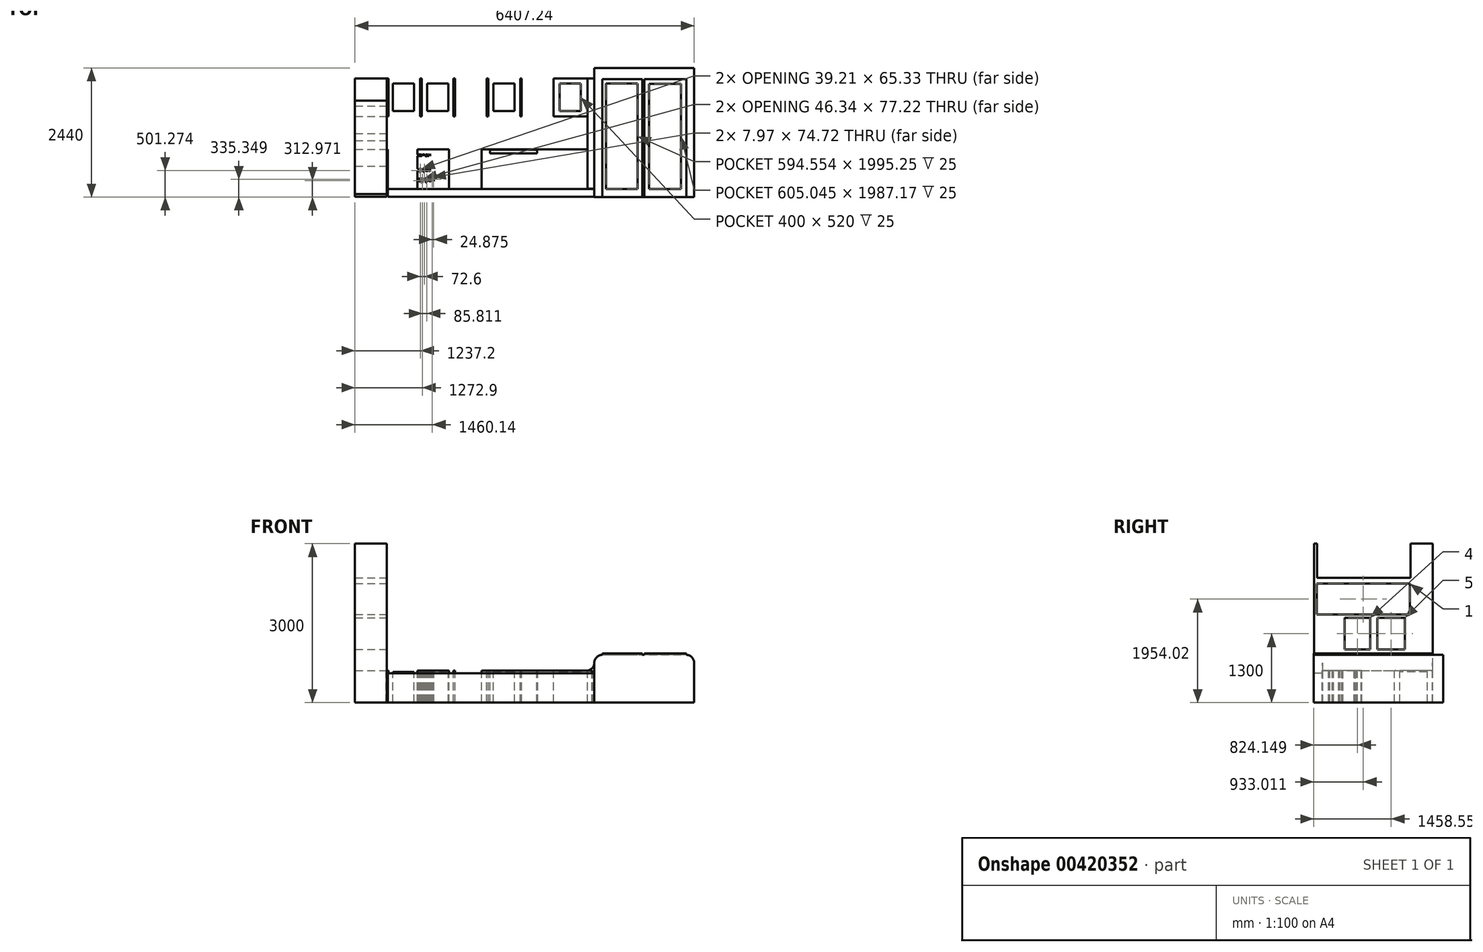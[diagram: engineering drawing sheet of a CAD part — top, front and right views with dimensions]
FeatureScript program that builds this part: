
annotation { "Feature Type Name" : "Feature", "Feature Type Description" : "" }
export const myFeature = defineFeature(function(context is Context, id is Id, definition is map)
    precondition{}
    {
        {
            var Q0;
            Q0=qCreatedBy(makeId("Top.planeOp"),FACE);
            var sketch = newSketch(context, id + "F0", { "sketchPlane" : qUnion([Q0])});
            skLineSegment(sketch, "E0.bottom", {"start": v(0, 750) * mm, "end": v(1806, 750) * mm});
            skLineSegment(sketch, "E0.top", {"start": v(0, 0) * mm, "end": v(3890, 0) * mm});
            skLineSegment(sketch, "E0.left", {"start": v(0, 750) * mm, "end": v(0, 0) * mm});
            skLineSegment(sketch, "E0.right", {"start": v(3890, 750) * mm, "end": v(3890, 0) * mm});
            skLineSegment(sketch, "E1.bottom", {"start": v(1190, 750) * mm, "end": v(1790, 750) * mm});
            skLineSegment(sketch, "E1.top", {"start": v(1190, 0) * mm, "end": v(1790, 0) * mm});
            skLineSegment(sketch, "E1.left", {"start": v(1190, 750) * mm, "end": v(1190, 0) * mm});
            skLineSegment(sketch, "E1.right", {"start": v(1790, 750) * mm, "end": v(1790, 0) * mm});
            skLineSegment(sketch, "E2.bottom", {"start": v(600, 740) * mm, "end": v(1164, 740) * mm});
            skLineSegment(sketch, "E2.top", {"start": v(600, 590) * mm, "end": v(1164, 590) * mm});
            skLineSegment(sketch, "E2.left", {"start": v(600, 740) * mm, "end": v(600, 590) * mm});
            skLineSegment(sketch, "E2.right", {"start": v(1164, 740) * mm, "end": v(1164, 590) * mm});
            skLineSegment(sketch, "E3.bottom", {"start": v(600, 560) * mm, "end": v(1164, 560) * mm});
            skLineSegment(sketch, "E3.top", {"start": v(600, 300) * mm, "end": v(1164, 300) * mm});
            skLineSegment(sketch, "E3.left", {"start": v(600, 560) * mm, "end": v(600, 300) * mm});
            skLineSegment(sketch, "E3.right", {"start": v(1164, 560) * mm, "end": v(1164, 300) * mm});
            skLineSegment(sketch, "E4.bottom", {"start": v(600, 270) * mm, "end": v(1164, 270) * mm});
            skLineSegment(sketch, "E4.top", {"start": v(600, 10) * mm, "end": v(1164, 10) * mm});
            skLineSegment(sketch, "E4.left", {"start": v(600, 270) * mm, "end": v(600, 10) * mm});
            skLineSegment(sketch, "E4.right", {"start": v(1164, 270) * mm, "end": v(1164, 10) * mm});
            skLineSegment(sketch, "E5.top", {"start": v(1816, 590) * mm, "end": v(2843, 590) * mm});
            skLineSegment(sketch, "E5.left", {"start": v(1816, 740) * mm, "end": v(1816, 590) * mm});
            skLineSegment(sketch, "E5.right", {"start": v(2843, 740) * mm, "end": v(2843, 590) * mm});
            skLineSegment(sketch, "E6.top", {"start": v(1816, 300) * mm, "end": v(2843, 300) * mm});
            skLineSegment(sketch, "E6.right", {"start": v(2843, 750) * mm, "end": v(2843, 590) * mm});
            skLineSegment(sketch, "E7.bottom", {"start": v(1826, 270) * mm, "end": v(2843, 270) * mm});
            skLineSegment(sketch, "E7.top", {"start": v(1826, 10) * mm, "end": v(2843, 10) * mm});
            skLineSegment(sketch, "E7.left", {"start": v(1826, 270) * mm, "end": v(1826, 10) * mm});
            skLineSegment(sketch, "E7.right", {"start": v(2843, 270) * mm, "end": v(2843, 10) * mm});
            skLineSegment(sketch, "E8.bottom", {"start": v(2853, 740) * mm, "end": v(3880, 740) * mm});
            skLineSegment(sketch, "E8.top", {"start": v(2853, 590) * mm, "end": v(3880, 590) * mm});
            skLineSegment(sketch, "E8.left", {"start": v(2853, 740) * mm, "end": v(2853, 590) * mm});
            skLineSegment(sketch, "E9.bottom", {"start": v(2853, 560) * mm, "end": v(3880, 560) * mm});
            skLineSegment(sketch, "E9.top", {"start": v(2853, 300) * mm, "end": v(3880, 300) * mm});
            skLineSegment(sketch, "E9.left", {"start": v(2853, 560) * mm, "end": v(2853, 300) * mm});
            skLineSegment(sketch, "E9.right", {"start": v(3880, 560) * mm, "end": v(3880, 300) * mm});
            skLineSegment(sketch, "E10.bottom", {"start": v(2853, 270) * mm, "end": v(3880, 270) * mm});
            skLineSegment(sketch, "E10.top", {"start": v(2853, 10) * mm, "end": v(3880, 10) * mm});
            skLineSegment(sketch, "E10.left", {"start": v(2853, 270) * mm, "end": v(2853, 10) * mm});
            skLineSegment(sketch, "E10.right", {"start": v(3880, 270) * mm, "end": v(3880, 10) * mm});
            skLineSegment(sketch, "E11.bottom", {"start": v(12.85, 1370) * mm, "end": v(3902.85, 1370) * mm});
            skLineSegment(sketch, "E11.top", {"start": v(12.85, 2090) * mm, "end": v(3902.85, 2090) * mm});
            skLineSegment(sketch, "E11.left", {"start": v(12.85, 1370) * mm, "end": v(12.85, 2090) * mm});
            skLineSegment(sketch, "E11.right", {"start": v(3902.85, 1370) * mm, "end": v(3902.85, 2090) * mm});
            skText(sketch, "E12", { "text": "Dishwasher", "fontName": "OpenSans-Regular.ttf"});
            skLineSegment(sketch, "E13", {"start": v(1174, 750) * mm, "end": v(1174, 0) * mm});
            skLineSegment(sketch, "E14", {"start": v(1806, 750) * mm, "end": v(1806, 0) * mm});
            skLineSegment(sketch, "E15", {"start": v(1816, 740) * mm, "end": v(2843, 740) * mm});
            skLineSegment(sketch, "E16", {"start": v(3890, 750) * mm, "end": v(1806, 750) * mm});
            skLineSegment(sketch, "E17", {"start": v(3880, 590) * mm, "end": v(3880, 740) * mm});
            skLineSegment(sketch, "E18", {"start": v(1816, 300) * mm, "end": v(1816, 560) * mm});
            skLineSegment(sketch, "E19", {"start": v(1816, 560) * mm, "end": v(2843, 560) * mm});
            skLineSegment(sketch, "E20.trimOffspring", {"start": v(2843, 560) * mm, "end": v(2843, 300) * mm});
            skLineSegment(sketch, "E21.bottom", {"start": v(42.85, 2090) * mm, "end": v(642.85, 2090) * mm});
            skLineSegment(sketch, "E21.top", {"start": v(42.85, 1370) * mm, "end": v(642.85, 1370) * mm});
            skLineSegment(sketch, "E21.left", {"start": v(42.85, 2090) * mm, "end": v(42.85, 1370) * mm});
            skLineSegment(sketch, "E21.right", {"start": v(642.85, 2090) * mm, "end": v(642.85, 1370) * mm});
            skLineSegment(sketch, "E22", {"start": v(6000, -150) * mm, "end": v(6000, 2090) * mm, "construction": true});
            skPoint(sketch, "E23", {"position": v(6000, 0) * mm});
            skPoint(sketch, "E24", {"position": v(6000, 1370) * mm});
            skPoint(sketch, "E25", {"position": v(6000, 750) * mm});
            skPoint(sketch, "E26", {"position": v(6000, 770) * mm});
            skLineSegment(sketch, "E27", {"start": v(6000, 2090) * mm, "end": v(5702.85, 2090) * mm, "construction": true});
            skLineSegment(sketch, "E28", {"start": v(6000, 2090) * mm, "end": v(6000, 2090) * mm});
            skLineSegment(sketch, "E29.bottom", {"start": v(672.85, 2090) * mm, "end": v(1272.85, 2090) * mm});
            skLineSegment(sketch, "E29.top", {"start": v(672.85, 1370) * mm, "end": v(1272.85, 1370) * mm});
            skLineSegment(sketch, "E29.left", {"start": v(672.85, 2090) * mm, "end": v(672.85, 1370) * mm});
            skLineSegment(sketch, "E29.right", {"start": v(1272.85, 2090) * mm, "end": v(1272.85, 1370) * mm});
            skLineSegment(sketch, "E30.bottom", {"start": v(1302.85, 2090) * mm, "end": v(1902.85, 2090) * mm});
            skLineSegment(sketch, "E30.top", {"start": v(1302.85, 1370) * mm, "end": v(1902.85, 1370) * mm});
            skLineSegment(sketch, "E30.left", {"start": v(1302.85, 2090) * mm, "end": v(1302.85, 1370) * mm});
            skLineSegment(sketch, "E30.right", {"start": v(1902.85, 2090) * mm, "end": v(1902.85, 1370) * mm});
            skLineSegment(sketch, "E31.bottom", {"start": v(1932.85, 2090) * mm, "end": v(2532.85, 2090) * mm});
            skLineSegment(sketch, "E31.top", {"start": v(1932.85, 1370) * mm, "end": v(2532.85, 1370) * mm});
            skLineSegment(sketch, "E31.left", {"start": v(1932.85, 2090) * mm, "end": v(1932.85, 1370) * mm});
            skLineSegment(sketch, "E31.right", {"start": v(2532.85, 2090) * mm, "end": v(2532.85, 1370) * mm});
            skLineSegment(sketch, "E32.bottom", {"start": v(2562.85, 2090) * mm, "end": v(3162.85, 2090) * mm});
            skLineSegment(sketch, "E32.top", {"start": v(2562.85, 1370) * mm, "end": v(3162.85, 1370) * mm});
            skLineSegment(sketch, "E32.left", {"start": v(2562.85, 2090) * mm, "end": v(2562.85, 1370) * mm});
            skLineSegment(sketch, "E32.right", {"start": v(3162.85, 2090) * mm, "end": v(3162.85, 1370) * mm});
            skLineSegment(sketch, "E33.bottom", {"start": v(3162.85, 2090) * mm, "end": v(3192.85, 2090) * mm});
            skLineSegment(sketch, "E33.top", {"start": v(3162.85, 1370) * mm, "end": v(3192.85, 1370) * mm});
            skLineSegment(sketch, "E33.left", {"start": v(3192.85, 2090) * mm, "end": v(3192.85, 1370) * mm});
            skLineSegment(sketch, "E34.bottom", {"start": v(3192.85, 2090) * mm, "end": v(3792.85, 2090) * mm});
            skLineSegment(sketch, "E34.top", {"start": v(3192.85, 1370) * mm, "end": v(3792.85, 1370) * mm});
            skLineSegment(sketch, "E34.right", {"start": v(3792.85, 2090) * mm, "end": v(3792.85, 1370) * mm});
            skLineSegment(sketch, "E35.bottom", {"start": v(30, 750) * mm, "end": v(590, 750) * mm});
            skLineSegment(sketch, "E35.top", {"start": v(30, 0) * mm, "end": v(590, 0) * mm});
            skLineSegment(sketch, "E35.left", {"start": v(30, 750) * mm, "end": v(30, 0) * mm});
            skLineSegment(sketch, "E35.right", {"start": v(590, 750) * mm, "end": v(590, 0) * mm});
            skText(sketch, "E36", { "text": "Lemans II \n541.32.620", "fontName": "OpenSans-Regular.ttf"});
            skText(sketch, "E37", { "text": "Bottom pull", "fontName": "OpenSans-Regular.ttf"});
            skText(sketch, "E38", { "text": "top pull", "fontName": "OpenSans-Regular.ttf"});
            skText(sketch, "E39", { "text": "top pull", "fontName": "OpenSans-Regular.ttf"});
            skLineSegment(sketch, "E40", {"start": v(6000, -150) * mm, "end": v(0, -150) * mm, "construction": true});
            skLineSegment(sketch, "E41.bottom", {"start": v(3902.85, 2090) * mm, "end": v(5702.85, 2090) * mm});
            skLineSegment(sketch, "E41.top", {"start": v(3902.85, 0) * mm, "end": v(5702.85, 0) * mm});
            skLineSegment(sketch, "E41.left", {"start": v(3902.85, 2090) * mm, "end": v(3902.85, 0) * mm});
            skLineSegment(sketch, "E41.right", {"start": v(5702.85, 2090) * mm, "end": v(5702.85, 0) * mm});
            skLineSegment(sketch, "E42", {"start": v(4772.85, 2090) * mm, "end": v(4772.85, 0) * mm});
            skLineSegment(sketch, "E43", {"start": v(4802.85, 2090) * mm, "end": v(4802.85, 0) * mm});
            skLineSegment(sketch, "E44", {"start": v(3932.85, 2090) * mm, "end": v(3932.85, 0) * mm});
            skLineSegment(sketch, "E45.bottom", {"start": v(127.34, 1990) * mm, "end": v(527.34, 1990) * mm});
            skLineSegment(sketch, "E45.top", {"start": v(127.34, 1470) * mm, "end": v(527.34, 1470) * mm});
            skLineSegment(sketch, "E45.left", {"start": v(127.34, 1990) * mm, "end": v(127.34, 1470) * mm});
            skLineSegment(sketch, "E45.right", {"start": v(527.34, 1990) * mm, "end": v(527.34, 1470) * mm});
            skLineSegment(sketch, "E46.bottom", {"start": v(772.85, 1990) * mm, "end": v(1172.85, 1990) * mm});
            skLineSegment(sketch, "E46.top", {"start": v(772.85, 1470) * mm, "end": v(1172.85, 1470) * mm});
            skLineSegment(sketch, "E46.left", {"start": v(772.85, 1990) * mm, "end": v(772.85, 1470) * mm});
            skLineSegment(sketch, "E46.right", {"start": v(1172.85, 1990) * mm, "end": v(1172.85, 1470) * mm});
            skLineSegment(sketch, "E47.bottom", {"start": v(2028.05, 1990) * mm, "end": v(2428.05, 1990) * mm});
            skLineSegment(sketch, "E47.top", {"start": v(2028.05, 1470) * mm, "end": v(2428.05, 1470) * mm});
            skLineSegment(sketch, "E47.left", {"start": v(2028.05, 1990) * mm, "end": v(2028.05, 1470) * mm});
            skLineSegment(sketch, "E47.right", {"start": v(2428.05, 1990) * mm, "end": v(2428.05, 1470) * mm});
            skLineSegment(sketch, "E48.bottom", {"start": v(3280.66, 1990) * mm, "end": v(3680.66, 1990) * mm});
            skLineSegment(sketch, "E48.top", {"start": v(3280.66, 1470) * mm, "end": v(3680.66, 1470) * mm});
            skLineSegment(sketch, "E48.left", {"start": v(3280.66, 1990) * mm, "end": v(3280.66, 1470) * mm});
            skLineSegment(sketch, "E48.right", {"start": v(3680.66, 1990) * mm, "end": v(3680.66, 1470) * mm});
            skText(sketch, "E49", { "text": "Stove", "fontName": "OpenSans-Regular.ttf"});
            skPoint(sketch, "E50", {"position": v(2061.13, 1179.17) * mm});
            skPoint(sketch, "E51", {"position": v(2414.2, 750) * mm});
            skLineSegment(sketch, "E52.bottom", {"start": v(1964.2, 750) * mm, "end": v(2864.2, 750) * mm});
            skLineSegment(sketch, "E52.top", {"start": v(1964.2, 670) * mm, "end": v(2864.2, 670) * mm});
            skLineSegment(sketch, "E52.left", {"start": v(1964.2, 750) * mm, "end": v(1964.2, 670) * mm});
            skLineSegment(sketch, "E52.right", {"start": v(2864.2, 750) * mm, "end": v(2864.2, 670) * mm});
            skLineSegment(sketch, "E53.bottom", {"start": v(3932.85, 2090) * mm, "end": v(4091.6, 2090) * mm});
            skLineSegment(sketch, "E53.top", {"start": v(3932.85, -150) * mm, "end": v(4091.6, -150) * mm});
            skLineSegment(sketch, "E53.left", {"start": v(3932.85, 2090) * mm, "end": v(3932.85, -150) * mm});
            skLineSegment(sketch, "E53.right", {"start": v(4091.6, 2090) * mm, "end": v(4091.6, -150) * mm});
            skLineSegment(sketch, "E54.bottom", {"start": v(5586.52, 2090) * mm, "end": v(5820.09, 2090) * mm});
            skLineSegment(sketch, "E54.top", {"start": v(5586.52, -159.02) * mm, "end": v(5820.09, -159.02) * mm});
            skLineSegment(sketch, "E54.left", {"start": v(5586.52, 2090) * mm, "end": v(5586.52, -159.02) * mm});
            skLineSegment(sketch, "E54.right", {"start": v(5820.09, 2090) * mm, "end": v(5820.09, -159.02) * mm});
            skPoint(sketch, "E55.oppositeSnap0", {"position": v(5703.3, 2090) * mm});
            skLineSegment(sketch, "E55.bottom", {"start": v(3932.85, 2286.83) * mm, "end": v(5820.09, 2286.83) * mm});
            skLineSegment(sketch, "E55.top", {"start": v(3932.85, 2090) * mm, "end": v(5820.09, 2090) * mm});
            skLineSegment(sketch, "E55.left", {"start": v(3932.85, 2286.83) * mm, "end": v(3932.85, 2090) * mm});
            skLineSegment(sketch, "E55.right", {"start": v(5820.09, 2286.83) * mm, "end": v(5820.09, 2090) * mm});
            skLineSegment(sketch, "E56.trimOffspring", {"start": v(3932.85, 2090) * mm, "end": v(12.85, 2090) * mm, "construction": true});
            skLineSegment(sketch, "E57.trimOffspring", {"start": v(5586.52, 2090) * mm, "end": v(4091.6, 2090) * mm, "construction": true});
            skLineSegment(sketch, "E58.bottom", {"start": v(1405.73, 1990) * mm, "end": v(1817.16, 1990) * mm});
            skLineSegment(sketch, "E58.top", {"start": v(1405.73, 1470) * mm, "end": v(1817.16, 1470) * mm});
            skLineSegment(sketch, "E58.left", {"start": v(1405.73, 1990) * mm, "end": v(1405.73, 1470) * mm});
            skLineSegment(sketch, "E58.right", {"start": v(1817.16, 1990) * mm, "end": v(1817.16, 1470) * mm});
            skLineSegment(sketch, "E59.bottom", {"start": v(2646, 1990) * mm, "end": v(3066.6, 1990) * mm});
            skLineSegment(sketch, "E59.top", {"start": v(2646, 1470) * mm, "end": v(3066.6, 1470) * mm});
            skLineSegment(sketch, "E59.left", {"start": v(2646, 1990) * mm, "end": v(2646, 1470) * mm});
            skLineSegment(sketch, "E59.right", {"start": v(3066.6, 1990) * mm, "end": v(3066.6, 1470) * mm});
            skLineSegment(sketch, "E60.bottom", {"start": v(30, 0) * mm, "end": v(0, 0) * mm});
            skLineSegment(sketch, "E60.top", {"start": v(30, -150) * mm, "end": v(0, -150) * mm});
            skLineSegment(sketch, "E60.left", {"start": v(30, 0) * mm, "end": v(30, -150) * mm});
            skLineSegment(sketch, "E60.right", {"start": v(0, 0) * mm, "end": v(0, -150) * mm});
            skLineSegment(sketch, "E61.bottom", {"start": v(0, 0) * mm, "end": v(3932.85, 0) * mm});
            skLineSegment(sketch, "E61.top", {"start": v(0, -150) * mm, "end": v(3932.85, -150) * mm});
            skLineSegment(sketch, "E61.right", {"start": v(3932.85, 0) * mm, "end": v(3932.85, -150) * mm});
            skLineSegment(sketch, "E62.bottom", {"start": v(4091.6, 0) * mm, "end": v(5586.52, 0) * mm});
            skLineSegment(sketch, "E62.top", {"start": v(4091.6, -159.02) * mm, "end": v(5586.52, -159.02) * mm});
            skLineSegment(sketch, "E62.left", {"start": v(4091.6, 0) * mm, "end": v(4091.6, -159.02) * mm});
            skLineSegment(sketch, "E62.right", {"start": v(5586.52, 0) * mm, "end": v(5586.52, -159.02) * mm});
            const initialGuessF0  = {"E12": [1.29, 0.4978, 1, 0, 0.0522], "E36": [0.08, 0.61298, 1, 0, 0.04765], "E37": [0.54096, 0.62134, 1, 0, 0.03929], "E38": [0.54368, 0.33543, 1, 0, 0.0599], "E39": [0.56002, 0.14482, 1, 0, 0.0708], "E49": [1.91777, 1.09917, 1, 0, 0.08]};
            skSetInitialGuess(sketch, initialGuessF0);
            skSolve(sketch);
        }
        {
            var Q0;
            {var subQ0=sQuery(id+"F0.wireOp",EDGE,"E11.left");Q0=makeQuery(id+"F0.imprint","IMPRINT",FACE,{"disambiguationData":[TD([[makeQuery(id+"F0.imprint","IMPRINT",EDGE,{"derivedFrom":subQ0}),-1.0]])]});}
            var Q1;
            Q1=makeQuery(id+"F0.imprint","IMPRINT",FACE,{"disambiguationData":[TD([[makeQuery(id+"F0.imprint","IMPRINT",EDGE,{"derivedFrom":sQuery(id+"F0.wireOp",EDGE,"E21.bottom")}),-1.0]])]});
            var Q2;
            {var subQ0=sQuery(id+"F0.wireOp",EDGE,"E21.right");Q2=makeQuery(id+"F0.imprint","IMPRINT",FACE,{"disambiguationData":[TD([[makeQuery(id+"F0.imprint","IMPRINT",EDGE,{"derivedFrom":subQ0}),1.0]])]});}
            var Q3;
            Q3=makeQuery(id+"F0.imprint","IMPRINT",FACE,{"disambiguationData":[TD([[makeQuery(id+"F0.imprint","IMPRINT",EDGE,{"derivedFrom":sQuery(id+"F0.wireOp",EDGE,"E29.bottom")}),-1.0]])]});
            var Q4;
            Q4=makeQuery(id+"F0.imprint","IMPRINT",FACE,{"disambiguationData":[TD([[makeQuery(id+"F0.imprint","IMPRINT",EDGE,{"derivedFrom":sQuery(id+"F0.wireOp",EDGE,"E30.bottom")}),-1.0]])]});
            var Q5;
            Q5=makeQuery(id+"F0.imprint","IMPRINT",FACE,{"disambiguationData":[TD([[makeQuery(id+"F0.imprint","IMPRINT",EDGE,{"derivedFrom":sQuery(id+"F0.wireOp",EDGE,"E32.bottom")}),-1.0]])]});
            var Q6;
            {var subQ0=sQuery(id+"F0.wireOp",EDGE,"E31.right");Q6=makeQuery(id+"F0.imprint","IMPRINT",FACE,{"disambiguationData":[TD([[makeQuery(id+"F0.imprint","IMPRINT",EDGE,{"derivedFrom":subQ0}),1.0]])]});}
            var Q7;
            Q7=makeQuery(id+"F0.imprint","IMPRINT",FACE,{"disambiguationData":[TD([[makeQuery(id+"F0.imprint","IMPRINT",EDGE,{"derivedFrom":sQuery(id+"F0.wireOp",EDGE,"E32.right")}),1.0]])]});
            var Q8;
            Q8=makeQuery(id+"F0.imprint","IMPRINT",FACE,{"disambiguationData":[TD([[makeQuery(id+"F0.imprint","IMPRINT",EDGE,{"derivedFrom":sQuery(id+"F0.wireOp",EDGE,"E33.left")}),1.0]])]});
            var Q9;
            Q9=makeQuery(id+"F0.imprint","IMPRINT",FACE,{"disambiguationData":[TD([[makeQuery(id+"F0.imprint","IMPRINT",EDGE,{"derivedFrom":sQuery(id+"F0.wireOp",EDGE,"E48.bottom")}),-1.0]])]});
            var Q10;
            {var subQ3=sQuery(id+"F0.wireOp",EDGE,"E34.right");Q10=makeQuery(id+"F0.imprint","IMPRINT",FACE,{"disambiguationData":[TD([[makeQuery(id+"F0.imprint","IMPRINT",EDGE,{"derivedFrom":subQ3}),1.0]])]});}
            var Q11;
            {var subQ4=sQuery(id+"F0.wireOp",EDGE,"E41.bottom");Q11=makeQuery(id+"F0.imprint","IMPRINT",FACE,{"disambiguationData":[TD([[makeQuery(id+"F0.imprint","IMPRINT",EDGE,{"derivedFrom":subQ4}),-1.0]])]});}
            var Q12;
            {var subQ0=sQuery(id+"F0.wireOp",EDGE,"E53.left");var subQ1=sQuery(id+"F0.wireOp",EDGE,"E41.top");var subQ2=makeQuery(id+"F0.imprint","INTERSECT",VERTEX,{"derivedFrom":[subQ1,subQ0]});Q12=makeQuery(id+"F0.imprint","IMPRINT",FACE,{"disambiguationData":[TD([[makeQuery(id+"F0.imprint","IMPRINT",EDGE,{"disambiguationData":[TD([[subQ2,-1.0]])],"derivedFrom":subQ1}),1.0]])]});}
            var Q13;
            Q13=makeQuery(id+"F0.imprint","IMPRINT",FACE,{"disambiguationData":[TD([[makeQuery(id+"F0.imprint","IMPRINT",EDGE,{"derivedFrom":sQuery(id+"F0.wireOp",EDGE,"E55.bottom")}),-1.0]])]});
            var Q14;
            {var subQ0=sQuery(id+"F0.wireOp",EDGE,"E42");Q14=makeQuery(id+"F0.imprint","IMPRINT",FACE,{"disambiguationData":[TD([[makeQuery(id+"F0.imprint","IMPRINT",EDGE,{"derivedFrom":subQ0}),-1.0]])]});}
            var Q15;
            {var subQ0=sQuery(id+"F0.wireOp",EDGE,"E42");Q15=makeQuery(id+"F0.imprint","IMPRINT",FACE,{"disambiguationData":[TD([[makeQuery(id+"F0.imprint","IMPRINT",EDGE,{"derivedFrom":subQ0}),1.0]])]});}
            var Q16;
            Q16=makeQuery(id+"F0.imprint","IMPRINT",FACE,{"disambiguationData":[TD([[makeQuery(id+"F0.imprint","IMPRINT",EDGE,{"derivedFrom":sQuery(id+"F0.wireOp",EDGE,"E1.bottom")}),-1.0]])]});
            var Q17;
            {var subQ7=sQuery(id+"F0.wireOp",EDGE,"E5.top");Q17=makeQuery(id+"F0.imprint","IMPRINT",FACE,{"disambiguationData":[TD([[makeQuery(id+"F0.imprint","IMPRINT",EDGE,{"derivedFrom":subQ7}),1.0]])]});}
            var Q18;
            {var subQ0=sQuery(id+"F0.wireOp",EDGE,"E42");Q18=makeQuery(id+"F0.imprint","IMPRINT",FACE,{"disambiguationData":[TD([[makeQuery(id+"F0.imprint","IMPRINT",EDGE,{"derivedFrom":subQ0}),-1.0]])]});}
            var Q19;
            {var subQ0=sQuery(id+"F0.wireOp",EDGE,"E41.right");Q19=makeQuery(id+"F0.imprint","IMPRINT",FACE,{"disambiguationData":[TD([[makeQuery(id+"F0.imprint","IMPRINT",EDGE,{"derivedFrom":subQ0}),-1.0]])]});}
            var Q20;
            {var subQ0=sQuery(id+"F0.wireOp",EDGE,"E43");Q20=makeQuery(id+"F0.imprint","IMPRINT",FACE,{"disambiguationData":[TD([[makeQuery(id+"F0.imprint","IMPRINT",EDGE,{"derivedFrom":subQ0}),1.0]])]});}
            var Q21;
            {var subQ4=sQuery(id+"F0.wireOp",EDGE,"E41.right");Q21=makeQuery(id+"F0.imprint","IMPRINT",FACE,{"disambiguationData":[TD([[makeQuery(id+"F0.imprint","IMPRINT",EDGE,{"derivedFrom":subQ4}),1.0]])]});}
            var Q22;
            {var subQ1=sQuery(id+"F0.wireOp",EDGE,"E8.top");Q22=makeQuery(id+"F0.imprint","IMPRINT",FACE,{"disambiguationData":[TD([[makeQuery(id+"F0.imprint","IMPRINT",EDGE,{"derivedFrom":subQ1}),1.0]])]});}
            var Q23;
            Q23=makeQuery(id+"F0.imprint","IMPRINT",FACE,{"disambiguationData":[TD([[makeQuery(id+"F0.imprint","IMPRINT",EDGE,{"derivedFrom":sQuery(id+"F0.wireOp",EDGE,"E9.bottom")}),-1.0]])]});
            var Q24;
            Q24=makeQuery(id+"F0.imprint","IMPRINT",FACE,{"disambiguationData":[TD([[makeQuery(id+"F0.imprint","IMPRINT",EDGE,{"derivedFrom":sQuery(id+"F0.wireOp",EDGE,"E10.bottom")}),-1.0]])]});
            var Q25;
            Q25=makeQuery(id+"F0.imprint","IMPRINT",FACE,{"disambiguationData":[TD([[makeQuery(id+"F0.imprint","IMPRINT",EDGE,{"derivedFrom":sQuery(id+"F0.wireOp",EDGE,"E7.bottom")}),-1.0]])]});
            var Q26;
            Q26=makeQuery(id+"F0.imprint","IMPRINT",FACE,{"disambiguationData":[TD([[makeQuery(id+"F0.imprint","IMPRINT",EDGE,{"derivedFrom":sQuery(id+"F0.wireOp",EDGE,"E6.top")}),1.0]])]});
            var Q27;
            {var subQ0=sQuery(id+"F0.wireOp",EDGE,"E15");var subQ1=sQuery(id+"F0.wireOp",EDGE,"E6.right");var subQ2=makeQuery(id+"F0.imprint","INTERSECT",VERTEX,{"derivedFrom":[subQ1,subQ0]});Q27=makeQuery(id+"F0.imprint","IMPRINT",FACE,{"disambiguationData":[TD([[makeQuery(id+"F0.imprint","IMPRINT",EDGE,{"disambiguationData":[TD([[subQ2,-1.0]])],"derivedFrom":subQ1}),-1.0]])]});}
            var Q28;
            {var subQ7=sQuery(id+"F0.wireOp",EDGE,"E3.bottom");Q28=makeQuery(id+"F0.imprint","IMPRINT",FACE,{"disambiguationData":[TD([[makeQuery(id+"F0.imprint","IMPRINT",EDGE,{"derivedFrom":subQ7}),-1.0]])]});}
            var Q29;
            {var subQ8=sQuery(id+"F0.wireOp",EDGE,"E2.bottom");Q29=makeQuery(id+"F0.imprint","IMPRINT",FACE,{"disambiguationData":[TD([[makeQuery(id+"F0.imprint","IMPRINT",EDGE,{"derivedFrom":subQ8}),-1.0]])]});}
            var Q30;
            Q30=makeQuery(id+"F0.imprint","IMPRINT",FACE,{"disambiguationData":[TD([[makeQuery(id+"F0.imprint","IMPRINT",EDGE,{"derivedFrom":sQuery(id+"F0.wireOp",EDGE,"E4.bottom")}),-1.0]])]});
            var Q31;
            {var subQ14=sQuery(id+"F0.wireOp",EDGE,"E35.bottom");Q31=makeQuery(id+"F0.imprint","IMPRINT",FACE,{"disambiguationData":[TD([[makeQuery(id+"F0.imprint","IMPRINT",EDGE,{"derivedFrom":subQ14}),-1.0]])]});}
            var Q32;
            {var subQ0=sQuery(id+"F0.wireOp",EDGE,"E0.left");Q32=makeQuery(id+"F0.imprint","IMPRINT",FACE,{"disambiguationData":[TD([[makeQuery(id+"F0.imprint","IMPRINT",EDGE,{"derivedFrom":subQ0}),1.0]])]});}
            var Q33;
            Q33=makeQuery(id+"F0.imprint","IMPRINT",FACE,{"disambiguationData":[TD([[makeQuery(id+"F0.imprint","IMPRINT",EDGE,{"derivedFrom":sQuery(id+"F0.wireOp",EDGE,"E45.bottom")}),-1.0]])]});
            var Q34;
            Q34=makeQuery(id+"F0.imprint","IMPRINT",FACE,{"disambiguationData":[TD([[makeQuery(id+"F0.imprint","IMPRINT",EDGE,{"derivedFrom":sQuery(id+"F0.wireOp",EDGE,"E46.bottom")}),-1.0]])]});
            var Q35;
            Q35=makeQuery(id+"F0.imprint","IMPRINT",FACE,{"disambiguationData":[TD([[makeQuery(id+"F0.imprint","IMPRINT",EDGE,{"derivedFrom":sQuery(id+"F0.wireOp",EDGE,"E31.bottom")}),-1.0]])]});
            var Q36;
            Q36=makeQuery(id+"F0.imprint","IMPRINT",FACE,{"disambiguationData":[TD([[makeQuery(id+"F0.imprint","IMPRINT",EDGE,{"derivedFrom":sQuery(id+"F0.wireOp",EDGE,"E47.bottom")}),-1.0]])]});
            var Q37;
            {var subQ5=sQuery(id+"F0.wireOp",EDGE,"E53.top");Q37=makeQuery(id+"F0.imprint","IMPRINT",FACE,{"disambiguationData":[TD([[makeQuery(id+"F0.imprint","IMPRINT",EDGE,{"derivedFrom":subQ5}),1.0]])]});}
            var Q38;
            {var subQ0=sQuery(id+"F0.wireOp",EDGE,"E29.right");Q38=makeQuery(id+"F0.imprint","IMPRINT",FACE,{"disambiguationData":[TD([[makeQuery(id+"F0.imprint","IMPRINT",EDGE,{"derivedFrom":subQ0}),1.0]])]});}
            var Q39;
            {var subQ0=sQuery(id+"F0.wireOp",EDGE,"E30.right");Q39=makeQuery(id+"F0.imprint","IMPRINT",FACE,{"disambiguationData":[TD([[makeQuery(id+"F0.imprint","IMPRINT",EDGE,{"derivedFrom":subQ0}),1.0]])]});}
            var Q40;
            {var subQ0=sQuery(id+"F0.wireOp",EDGE,"E0.right");Q40=makeQuery(id+"F0.imprint","IMPRINT",FACE,{"disambiguationData":[TD([[makeQuery(id+"F0.imprint","IMPRINT",EDGE,{"derivedFrom":subQ0}),-1.0]])]});}
            var Q41;
            {var subQ0=sQuery(id+"F0.wireOp",EDGE,"E8.left");var subQ1=sQuery(id+"F0.wireOp",EDGE,"E8.bottom");var subQ2=makeQuery(id+"F0.imprint","INTERSECT",VERTEX,{"derivedFrom":[subQ1,subQ0]});Q41=makeQuery(id+"F0.imprint","IMPRINT",FACE,{"disambiguationData":[TD([[makeQuery(id+"F0.imprint","IMPRINT",EDGE,{"disambiguationData":[TD([[subQ2,-1.0]])],"derivedFrom":subQ1}),-1.0]])]});}
            var Q42;
            {var subQ0=sQuery(id+"F0.wireOp",EDGE,"E1.left");Q42=makeQuery(id+"F0.imprint","IMPRINT",FACE,{"disambiguationData":[TD([[makeQuery(id+"F0.imprint","IMPRINT",EDGE,{"derivedFrom":subQ0}),-1.0]])]});}
            var Q43;
            {var subQ30=sQuery(id+"F0.wireOp",EDGE,"E2.bottom");Q43=makeQuery(id+"F0.imprint","IMPRINT",FACE,{"disambiguationData":[TD([[makeQuery(id+"F0.imprint","IMPRINT",EDGE,{"derivedFrom":subQ30}),1.0]])]});}
            extrude(context, id + "F1", {"entities" : qUnion([Q0, Q1, Q2, Q3, Q4, Q5, Q6, Q7, Q8, Q9, Q10, Q11, Q12, Q13, Q14, Q15, Q16, Q17, Q18, Q19, Q20, Q21, Q22, Q23, Q24, Q25, Q26, Q27, Q28, Q29, Q30, Q31, Q32, Q33, Q34, Q35, Q36, Q37, Q38, Q39, Q40, Q41, Q42, Q43]), "oppositeDirection" : true, "depth" : 600 * mm});
        }
        {
            var Q0;
            Q0=makeQuery(id+"F1.opExtrude","SWEPT_FACE",FACE,{"disambiguationData":[OSD([sQuery(id+"F0.wireOp",EDGE,"E55.bottom")])]});
            var sketch = newSketch(context, id + "F2", { "sketchPlane" : qUnion([Q0])});
            skLineSegment(sketch, "E63.bottom", {"start": v(-3932.85, -600) * mm, "end": v(-5820.09, -600) * mm});
            skLineSegment(sketch, "E63.top", {"start": v(-4082.85, 300) * mm, "end": v(-5670.09, 300) * mm});
            skLineSegment(sketch, "E63.left", {"start": v(-3932.85, 150) * mm, "end": v(-3932.85, 150) * mm});
            skLineSegment(sketch, "E63.right", {"start": v(-5820.09, -600) * mm, "end": v(-5820.09, 150) * mm});
            skPoint(sketch, "E64.visualSharp", {"position": v(-3932.85, 300) * mm});
            skArc(sketch, "E64.filletArc", {"start": v(-3932.85, 150) * mm, "mid": v(-3976.78, 256.07) * mm, "end": v(-4082.85, 300) * mm});
            skPoint(sketch, "E65.visualSharp", {"position": v(-5820.09, 300) * mm});
            skArc(sketch, "E65.filletArc", {"start": v(-5670.09, 300) * mm, "mid": v(-5776.15, 256.07) * mm, "end": v(-5820.09, 150) * mm});
            skPoint(sketch, "E66.visualSharp", {"position": v(-3932.85, 0) * mm});
            skLineSegment(sketch, "E67.bottom", {"start": v(-3932.85, -600) * mm, "end": v(-3803.33, -600) * mm});
            skLineSegment(sketch, "E67.left", {"start": v(-3932.85, -600) * mm, "end": v(-3932.85, 150) * mm});
            skLineSegment(sketch, "E67.right", {"start": v(-3803.33, -600) * mm, "end": v(-3803.33, 1.4) * mm});
            skLineSegment(sketch, "E68", {"start": v(-3782.85, 0) * mm, "end": v(-3782.85, 0) * mm});
            skArc(sketch, "E69.filletArc", {"start": v(-3932.85, 150) * mm, "mid": v(-3895.92, 51.44) * mm, "end": v(-3803.33, 1.4) * mm});
            skPoint(sketch, "E67.top.end.orphan", {"position": v(-3803.33, 150) * mm});
            skPoint(sketch, "E70.bottom.start.orphan", {"position": v(-3766.85, 0) * mm});
            skSolve(sketch);
        }
        {
            var Q0;
            Q0=makeQuery(id+"F2.imprint","IMPRINT",FACE,{"disambiguationData":[TD([[makeQuery(id+"F2.imprint","IMPRINT",EDGE,{"derivedFrom":sQuery(id+"F2.wireOp",EDGE,"E63.top")}),1.0]])]});
            var Q1;
            {var subQ0=sQuery(id+"F2.wireOp",EDGE,"E63.bottom");Q1=makeQuery(id+"F2.imprint","IMPRINT",FACE,{"disambiguationData":[TD([[makeQuery(id+"F2.imprint","IMPRINT",EDGE,{"derivedFrom":subQ0}),-1.0]])]});}
            extrude(context, id + "F3", {"entities" : qUnion([Q0, Q1]), "operationType" : NewBodyOperationType.ADD, "oppositeDirection" : true, "depth" : 2440 * mm});
        }
        {
            var Q0;
            Q0=makeQuery(id+"F3.opExtrude","SWEPT_FACE",FACE,{"disambiguationData":[OSD([sQuery(id+"F2.wireOp",EDGE,"E63.top")])]});
            var sketch = newSketch(context, id + "F4", { "sketchPlane" : qUnion([Q0])});
            skLineSegment(sketch, "E71.bottom", {"start": v(4082.85, 2073.08) * mm, "end": v(4839.76, 2073.08) * mm});
            skLineSegment(sketch, "E71.top", {"start": v(4082.85, -153.17) * mm, "end": v(4839.76, -153.17) * mm});
            skLineSegment(sketch, "E71.left", {"start": v(4082.85, 2073.08) * mm, "end": v(4082.85, -153.17) * mm});
            skLineSegment(sketch, "E71.right", {"start": v(4839.76, 2073.08) * mm, "end": v(4839.76, -153.17) * mm});
            skLineSegment(sketch, "E72.bottom", {"start": v(5670.09, 2074.07) * mm, "end": v(4876.47, 2074.07) * mm});
            skLineSegment(sketch, "E72.top", {"start": v(5670.09, -153.17) * mm, "end": v(4876.47, -153.17) * mm});
            skLineSegment(sketch, "E72.left", {"start": v(5670.09, 2074.07) * mm, "end": v(5670.09, -153.17) * mm});
            skLineSegment(sketch, "E72.right", {"start": v(4876.47, 2074.07) * mm, "end": v(4876.47, -153.17) * mm});
            skLineSegment(sketch, "E73.bottom", {"start": v(4157.12, 1995.25) * mm, "end": v(4751.68, 1995.25) * mm});
            skLineSegment(sketch, "E73.top", {"start": v(4157.12, 0) * mm, "end": v(4751.68, 0) * mm});
            skLineSegment(sketch, "E73.left", {"start": v(4157.12, 1995.25) * mm, "end": v(4157.12, 0) * mm});
            skLineSegment(sketch, "E73.right", {"start": v(4751.68, 1995.25) * mm, "end": v(4751.68, 0) * mm});
            skLineSegment(sketch, "E74.bottom", {"start": v(4967.17, 1987.17) * mm, "end": v(5572.21, 1987.17) * mm});
            skLineSegment(sketch, "E74.top", {"start": v(4967.17, 0) * mm, "end": v(5572.21, 0) * mm});
            skLineSegment(sketch, "E74.left", {"start": v(4967.17, 1987.17) * mm, "end": v(4967.17, 0) * mm});
            skLineSegment(sketch, "E74.right", {"start": v(5572.21, 1987.17) * mm, "end": v(5572.21, 0) * mm});
            skSolve(sketch);
        }
        {
            var Q0;
            Q0=makeQuery(id+"F4.imprint","IMPRINT",FACE,{"disambiguationData":[TD([[makeQuery(id+"F4.imprint","IMPRINT",EDGE,{"derivedFrom":sQuery(id+"F4.wireOp",EDGE,"E71.bottom")}),-1.0]])]});
            var Q1;
            Q1=makeQuery(id+"F4.imprint","IMPRINT",FACE,{"disambiguationData":[TD([[makeQuery(id+"F4.imprint","IMPRINT",EDGE,{"derivedFrom":sQuery(id+"F4.wireOp",EDGE,"E72.bottom")}),1.0]])]});
            extrude(context, id + "F5", {"entities" : qUnion([Q0, Q1]), "operationType" : NewBodyOperationType.ADD, "depth" : 25 * mm});
        }
        {
            var Q0;
            {var subQ5=sQuery(id+"F2.wireOp",EDGE,"E67.bottom");Q0=makeQuery(id+"F2.imprint","IMPRINT",FACE,{"disambiguationData":[TD([[makeQuery(id+"F2.imprint","IMPRINT",EDGE,{"derivedFrom":subQ5}),1.0]])]});}
            extrude(context, id + "F6", {"entities" : qUnion([Q0]), "operationType" : NewBodyOperationType.ADD, "oppositeDirection" : true, "depth" : 2280 * mm, "hasSecondDirection" : true, "secondDirectionOppositeDirection" : true, "secondDirectionDepth" : 200 * mm});
        }
        {
            var Q0;
            Q0=makeQuery(id+"F0.imprint","IMPRINT",FACE,{"disambiguationData":[TD([[makeQuery(id+"F0.imprint","IMPRINT",EDGE,{"derivedFrom":sQuery(id+"F0.wireOp",EDGE,"E45.bottom")}),-1.0]])]});
            var Q1;
            Q1=makeQuery(id+"F0.imprint","IMPRINT",FACE,{"disambiguationData":[TD([[makeQuery(id+"F0.imprint","IMPRINT",EDGE,{"derivedFrom":sQuery(id+"F0.wireOp",EDGE,"E46.bottom")}),-1.0]])]});
            var Q2;
            Q2=makeQuery(id+"F0.imprint","IMPRINT",FACE,{"disambiguationData":[TD([[makeQuery(id+"F0.imprint","IMPRINT",EDGE,{"derivedFrom":sQuery(id+"F0.wireOp",EDGE,"E47.bottom")}),-1.0]])]});
            var Q3;
            Q3=makeQuery(id+"F0.imprint","IMPRINT",FACE,{"disambiguationData":[TD([[makeQuery(id+"F0.imprint","IMPRINT",EDGE,{"derivedFrom":sQuery(id+"F0.wireOp",EDGE,"E48.bottom")}),-1.0]])]});
            extrude(context, id + "F7", {"entities" : qUnion([Q0, Q1, Q2, Q3]), "operationType" : NewBodyOperationType.ADD, "oppositeDirection" : true, "depth" : 25 * mm});
        }
        {
            var Q0;
            Q0=makeQuery(id+"F0.imprint","IMPRINT",FACE,{"disambiguationData":[TD([[makeQuery(id+"F0.imprint","IMPRINT",EDGE,{"derivedFrom":sQuery(id+"F0.wireOp",EDGE,"E45.bottom")}),-1.0]])]});
            var Q1;
            Q1=makeQuery(id+"F0.imprint","IMPRINT",FACE,{"disambiguationData":[TD([[makeQuery(id+"F0.imprint","IMPRINT",EDGE,{"derivedFrom":sQuery(id+"F0.wireOp",EDGE,"E46.bottom")}),-1.0]])]});
            var Q2;
            Q2=makeQuery(id+"F0.imprint","IMPRINT",FACE,{"disambiguationData":[TD([[makeQuery(id+"F0.imprint","IMPRINT",EDGE,{"derivedFrom":sQuery(id+"F0.wireOp",EDGE,"E47.bottom")}),-1.0]])]});
            var Q3;
            Q3=makeQuery(id+"F0.imprint","IMPRINT",FACE,{"disambiguationData":[TD([[makeQuery(id+"F0.imprint","IMPRINT",EDGE,{"derivedFrom":sQuery(id+"F0.wireOp",EDGE,"E48.bottom")}),-1.0]])]});
            extrude(context, id + "F8", {"entities" : qUnion([Q0, Q1, Q2, Q3]), "operationType" : NewBodyOperationType.REMOVE, "oppositeDirection" : true, "depth" : 25 * mm});
        }
        {
            var Q0;
            {var subQ8=sQuery(id+"F0.wireOp",EDGE,"E60.left");Q0=makeQuery(id+"F0.imprint","IMPRINT",FACE,{"disambiguationData":[TD([[makeQuery(id+"F0.imprint","IMPRINT",EDGE,{"derivedFrom":subQ8}),1.0]])]});}
            extrude(context, id + "F9", {"entities" : qUnion([Q0]), "oppositeDirection" : true, "depth" : 600 * mm, "hasSecondDirection" : true, "secondDirectionOppositeDirection" : true, "secondDirectionDepth" : 50 * mm});
        }
        {
            var Q0;
            Q0=makeQuery(id+"F1.opExtrude","SWEPT_FACE",FACE,{"disambiguationData":[OSD([sQuery(id+"F0.wireOp",EDGE,"E11.left")])]});
            var sketch = newSketch(context, id + "F10", { "sketchPlane" : qUnion([Q0])});
            skLineSegment(sketch, "E75.bottom", {"start": v(150, -600) * mm, "end": v(-2090, -600) * mm});
            skLineSegment(sketch, "E75.top", {"start": v(150, 2400) * mm, "end": v(-2090, 2400) * mm});
            skLineSegment(sketch, "E75.left", {"start": v(150, -600) * mm, "end": v(150, 2400) * mm});
            skLineSegment(sketch, "E75.right", {"start": v(-2090, -600) * mm, "end": v(-2090, 2400) * mm});
            skLineSegment(sketch, "E76", {"start": v(-2090, 1700) * mm, "end": v(150, 1700) * mm});
            skLineSegment(sketch, "E77", {"start": v(-2090, 1000) * mm, "end": v(150, 1000) * mm});
            skLineSegment(sketch, "E78", {"start": v(-2090, 400) * mm, "end": v(150, 400) * mm});
            skLineSegment(sketch, "E79.bottom", {"start": v(-911.85, 1000) * mm, "end": v(-430.11, 1000) * mm});
            skLineSegment(sketch, "E79.top", {"start": v(-911.85, 400) * mm, "end": v(-430.11, 400) * mm});
            skLineSegment(sketch, "E79.left", {"start": v(-911.85, 1000) * mm, "end": v(-911.85, 400) * mm});
            skLineSegment(sketch, "E79.right", {"start": v(-430.11, 1000) * mm, "end": v(-430.11, 400) * mm});
            skLineSegment(sketch, "E80.bottom", {"start": v(-1565.39, 1000) * mm, "end": v(-1045.38, 1000) * mm});
            skLineSegment(sketch, "E80.top", {"start": v(-1565.39, 400) * mm, "end": v(-1045.38, 400) * mm});
            skLineSegment(sketch, "E80.left", {"start": v(-1565.39, 1000) * mm, "end": v(-1565.39, 400) * mm});
            skLineSegment(sketch, "E80.right", {"start": v(-1045.38, 1000) * mm, "end": v(-1045.38, 400) * mm});
            skLineSegment(sketch, "E81.bottom", {"start": v(-1457.7, 903.22) * mm, "end": v(-1161.3, 903.22) * mm});
            skLineSegment(sketch, "E81.top", {"start": v(-1457.7, 486.62) * mm, "end": v(-1161.3, 486.62) * mm});
            skLineSegment(sketch, "E81.left", {"start": v(-1457.7, 903.22) * mm, "end": v(-1457.7, 486.62) * mm});
            skLineSegment(sketch, "E81.right", {"start": v(-1161.3, 903.22) * mm, "end": v(-1161.3, 486.62) * mm});
            skLineSegment(sketch, "E82.bottom", {"start": v(-777.96, 892.58) * mm, "end": v(-507.08, 892.58) * mm});
            skLineSegment(sketch, "E82.top", {"start": v(-777.96, 468.78) * mm, "end": v(-507.08, 468.78) * mm});
            skLineSegment(sketch, "E82.left", {"start": v(-777.96, 892.58) * mm, "end": v(-777.96, 468.78) * mm});
            skLineSegment(sketch, "E82.right", {"start": v(-507.08, 892.58) * mm, "end": v(-507.08, 468.78) * mm});
            skLineSegment(sketch, "E83.bottom", {"start": v(-1661.57, 1646.06) * mm, "end": v(101.89, 1646.06) * mm});
            skLineSegment(sketch, "E83.top", {"start": v(-1661.57, 1061.99) * mm, "end": v(101.89, 1061.99) * mm});
            skLineSegment(sketch, "E83.left", {"start": v(-1661.57, 1646.06) * mm, "end": v(-1661.57, 1061.99) * mm});
            skLineSegment(sketch, "E83.right", {"start": v(101.89, 1646.06) * mm, "end": v(101.89, 1061.99) * mm});
            skLineSegment(sketch, "E84.bottom", {"start": v(-1670.76, 2400) * mm, "end": v(95.12, 2400) * mm});
            skLineSegment(sketch, "E84.top", {"start": v(-1670.76, 1756.87) * mm, "end": v(95.12, 1756.87) * mm});
            skLineSegment(sketch, "E84.left", {"start": v(-1670.76, 2400) * mm, "end": v(-1670.76, 1756.87) * mm});
            skLineSegment(sketch, "E84.right", {"start": v(95.12, 2400) * mm, "end": v(95.12, 1756.87) * mm});
            skLineSegment(sketch, "E85.bottom", {"start": v(-1370, -600) * mm, "end": v(-1370, -600) * mm});
            skLineSegment(sketch, "E85.top", {"start": v(-1370, 0) * mm, "end": v(-1370, 0) * mm});
            skLineSegment(sketch, "E85.left", {"start": v(-1370, -600) * mm, "end": v(-1370, 0) * mm});
            skLineSegment(sketch, "E85.right", {"start": v(-1370, -600) * mm, "end": v(-1370, 0) * mm});
            skLineSegment(sketch, "E86.bottom", {"start": v(-745.27, 0) * mm, "end": v(-1370, 0) * mm});
            skLineSegment(sketch, "E86.top", {"start": v(-745.27, -600) * mm, "end": v(-1370, -600) * mm});
            skLineSegment(sketch, "E86.left", {"start": v(-745.27, 0) * mm, "end": v(-745.27, -600) * mm});
            skLineSegment(sketch, "E86.right", {"start": v(-1370, 0) * mm, "end": v(-1370, -600) * mm});
            skSolve(sketch);
        }
        {
            var Q0;
            {var subQ0=sQuery(id+"F10.wireOp",EDGE,"E78");Q0=makeQuery(id+"F10.imprint","IMPRINT",FACE,{"disambiguationData":[TD([[makeQuery(id+"F10.imprint","IMPRINT",EDGE,{"derivedFrom":subQ0}),-1.0]])]});}
            var Q1;
            {var subQ0=sQuery(id+"F10.wireOp",EDGE,"E77");Q1=makeQuery(id+"F10.imprint","IMPRINT",FACE,{"disambiguationData":[TD([[makeQuery(id+"F10.imprint","IMPRINT",EDGE,{"derivedFrom":subQ0}),-1.0]])]});}
            var Q2;
            {var subQ0=sQuery(id+"F10.wireOp",EDGE,"E76");Q2=makeQuery(id+"F10.imprint","IMPRINT",FACE,{"disambiguationData":[TD([[makeQuery(id+"F10.imprint","IMPRINT",EDGE,{"derivedFrom":subQ0}),-1.0]])]});}
            var Q3;
            {var subQ0=sQuery(id+"F10.wireOp",EDGE,"E75.top");Q3=makeQuery(id+"F10.imprint","IMPRINT",FACE,{"disambiguationData":[TD([[makeQuery(id+"F10.imprint","IMPRINT",EDGE,{"derivedFrom":subQ0}),1.0]])]});}
            var Q4;
            {var subQ1=sQuery(id+"F0.wireOp",EDGE,"E11.left");var subQ5=makeQuery(id+"F1.opExtrude","CAP_EDGE",EDGE,{"disambiguationData":[OSD([subQ1])],"isStart":true});Q4=makeQuery(id+"F10.imprint","IMPRINT",FACE,{"disambiguationData":[TD([[makeQuery(id+"F10.imprint","IMPRINT",EDGE,{"derivedFrom":subQ5}),1.0]])]});}
            extrude(context, id + "F11", {"entities" : qUnion([Q0, Q1, Q2, Q3, Q4]), "depth" : 600 * mm});
        }
    });
